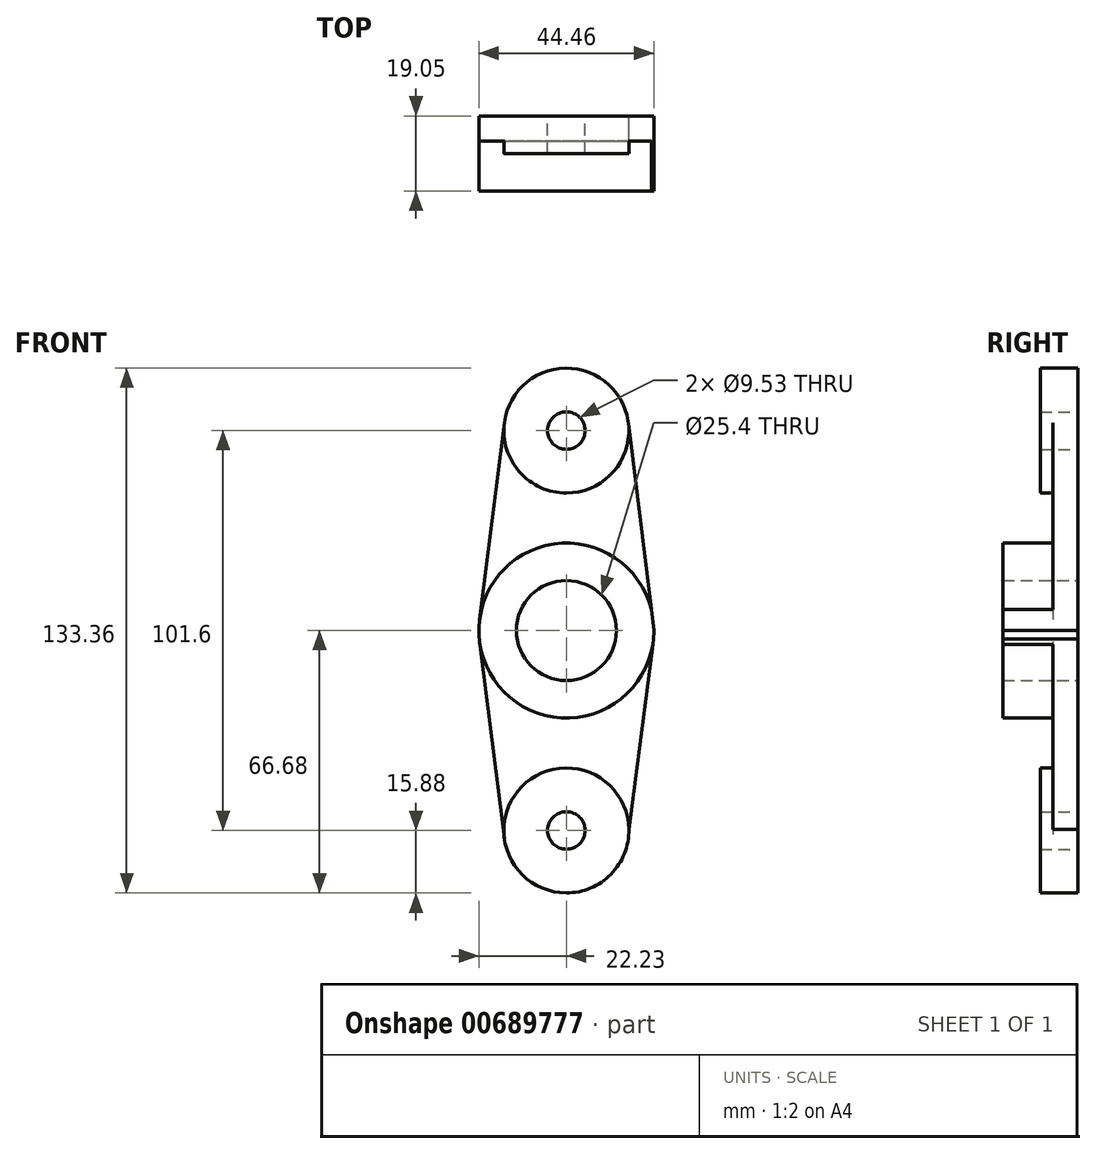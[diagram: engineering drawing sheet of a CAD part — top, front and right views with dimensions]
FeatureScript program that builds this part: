
annotation { "Feature Type Name" : "Feature", "Feature Type Description" : "" }
export const myFeature = defineFeature(function(context is Context, id is Id, definition is map)
    precondition{}
    {
        {
            var Q0;
            Q0=qCreatedBy(makeId("Front.planeOp"),FACE);
            var sketch = newSketch(context, id + "F0", { "sketchPlane" : qUnion([Q0])});
            skCircle(sketch, "E0", {"center": v(0, 0) * mm, "radius": 12.7 * mm});
            skCircle(sketch, "E1", {"center": v(0, 0) * mm, "radius": 22.23 * mm});
            skLineSegment(sketch, "E2", {"start": v(0, 0) * mm, "end": v(0, 50.8) * mm, "construction": true});
            skLineSegment(sketch, "E3", {"start": v(0, 0) * mm, "end": v(0, -50.8) * mm, "construction": true});
            skCircle(sketch, "E4", {"center": v(0, 50.8) * mm, "radius": 4.76 * mm});
            skCircle(sketch, "E5", {"center": v(0, -50.8) * mm, "radius": 4.76 * mm});
            skCircle(sketch, "E6", {"center": v(0, 50.8) * mm, "radius": 15.88 * mm});
            skCircle(sketch, "E7", {"center": v(0, -50.8) * mm, "radius": 15.88 * mm});
            skLineSegment(sketch, "E8", {"start": v(-15.75, 52.78) * mm, "end": v(-22.4, 0) * mm});
            skLineSegment(sketch, "E9", {"start": v(-22.4, 0) * mm, "end": v(-15.75, -52.78) * mm});
            skLineSegment(sketch, "E10", {"start": v(15.76, 52.73) * mm, "end": v(22.23, 0) * mm});
            skLineSegment(sketch, "E11", {"start": v(22.12, -2.15) * mm, "end": v(15.86, -50.61) * mm});
            skSolve(sketch);
        }
        {
            var Q0;
            Q0=makeQuery(id+"F0.imprint","IMPRINT",FACE,{"disambiguationData":[TD([[makeQuery(id+"F0.imprint","IMPRINT",EDGE,{"derivedFrom":sQuery(id+"F0.wireOp",EDGE,"E0")}),-1.0]])]});
            extrude(context, id + "F1", {"entities" : qUnion([Q0]), "depth" : 19.05 * mm, "offsetDistance" : 25.4 * mm});
        }
        {
            var Q0;
            {var subQ0=sQuery(id+"F0.wireOp",EDGE,"E10");var subQ1=sQuery(id+"F0.wireOp",EDGE,"E1");var subQ2=makeQuery(id+"F0.imprint","INTERSECT",VERTEX,{"disambiguationData":[OD(1.0)],"derivedFrom":[subQ1,subQ0]});Q0=makeQuery(id+"F0.imprint","IMPRINT",FACE,{"disambiguationData":[TD([[makeQuery(id+"F0.imprint","IMPRINT",EDGE,{"disambiguationData":[TD([[subQ2,-1.0]])],"derivedFrom":subQ1}),-1.0]])]});}
            var Q1;
            {var subQ0=sQuery(id+"F0.wireOp",EDGE,"E9");var subQ1=sQuery(id+"F0.wireOp",EDGE,"E1");var subQ2=makeQuery(id+"F0.imprint","INTERSECT",VERTEX,{"derivedFrom":[subQ1,subQ0]});Q1=makeQuery(id+"F0.imprint","IMPRINT",FACE,{"disambiguationData":[TD([[makeQuery(id+"F0.imprint","IMPRINT",EDGE,{"disambiguationData":[TD([[subQ2,-1.0]])],"derivedFrom":subQ1}),-1.0]])]});}
            extrude(context, id + "F2", {"entities" : qUnion([Q0, Q1]), "operationType" : NewBodyOperationType.ADD, "depth" : 6.35 * mm, "offsetDistance" : 25.4 * mm});
        }
        {
            var Q0;
            Q0=makeQuery(id+"F0.imprint","IMPRINT",FACE,{"disambiguationData":[TD([[makeQuery(id+"F0.imprint","IMPRINT",EDGE,{"derivedFrom":sQuery(id+"F0.wireOp",EDGE,"E4")}),-1.0]])]});
            var Q1;
            Q1=makeQuery(id+"F0.imprint","IMPRINT",FACE,{"disambiguationData":[TD([[makeQuery(id+"F0.imprint","IMPRINT",EDGE,{"derivedFrom":sQuery(id+"F0.wireOp",EDGE,"E5")}),-1.0]])]});
            extrude(context, id + "F3", {"entities" : qUnion([Q0, Q1]), "operationType" : NewBodyOperationType.ADD, "depth" : 9.52 * mm, "offsetDistance" : 25.4 * mm});
        }
    });
